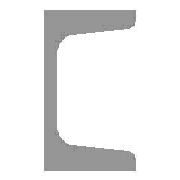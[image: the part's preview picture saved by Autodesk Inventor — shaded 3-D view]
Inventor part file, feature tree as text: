
AUTODESK INVENTOR PART (.ipt)
format: ipt  version: 2017 (Build 210142000, 142)  size: 141,824 bytes
history: native  units: mm (DEFAULTED — no unit token found)
features: other x4, plane x2, sketch x2, split x1
ambient origin geometry x8: Origin, YZ Plane, XZ Plane, XY Plane, X Axis, Y Axis, Z Axis, Center Point
bodies: Solid1 (feature_tree), Body (feature_tree)
feature tree (9):
  parser-record x1  (decoder bookkeeping rows leaked as tree rows — omitted from the tree; the rows remain in map.json)
  other  "Driven Length"
  other  "Start plane"
  other  "End plane"
  plane  "Work Plane4"
  split  "Split1"
  sketch  "Sketch3"  dims[d0=4.6736mm]
  plane  "Work Plane3"
  sketch  "Sketch4"  dims[d1=50.8mm d2=40.2336mm d3=7.5184mm d4=17.682845mm d5=0.926581mm d6=2438.4mm d7=0.0mm d25=0.0mm d26=-0.0mm d27=2438.4mm d28=6.712646mm d29=2.2352mm d30=90.0deg d31=2438.4mm]
